# Revit family: XL-MI-G-BO
name_source: partatom
category: Plumbing Fixtures
revit_build: Autodesk Revit 2018 (Build: 20170223_1515(x64)
units: mm (PartAtom-declared; Revit-internal decimal feet)

## family parameters
Always vertical = Yes
Cut with Voids When Loaded = No
Part Type = Normal
Room Calculation Point = No
Round Connector Dimension = Use Diameter
Shared = No
Work Plane-Based = No

## types (12) — shared parameters
Description = BOLT ON (FIXED) EXTENSIONS FOR XL-MI-G GREASE INTERCEPTORS
E- Height = 6 "
Manufacturer = MIFAB
URL = WWW.MIFAB.COM

## per-type parameters (varying)
| type | A-Length | B- Width |
| XL-MI-G-BO-0-10 | 42 " | 28 " |
| XL-MI-G-BO-1-10 | 55 " | 37 " |
| XL-MI-G-BO-2-10 | 58 " | 38 " |
| XL-MI-G-BO-3-10 | 61 " | 39 " |
| XL-MI-G-BO-4-10 | 70 " | 44 " |
| XL-MI-G-BO-5-10 | 75 " | 46 " |
| XL-MI-G-BO-6-10 | 77 " | 49 " |
| XL-MI-G-BO-7-10 | 80 " | 51 " |
| XL-MI-G-BO-8-10 | 84 " | 56 " |
| XL-MI-G-BO-9-10 | 92 " | 61 " |
| XL-MI-G-BO-10-10 | 102 " | 74 " |
| XL-MI-G-BO-11-10 | 108 " | 76 " |

note: column(s) folded — value = type name in every type: Model

## geometry (parser evidence)
native form markers: Sweep x2
no freeform markers — native parametric forms only
